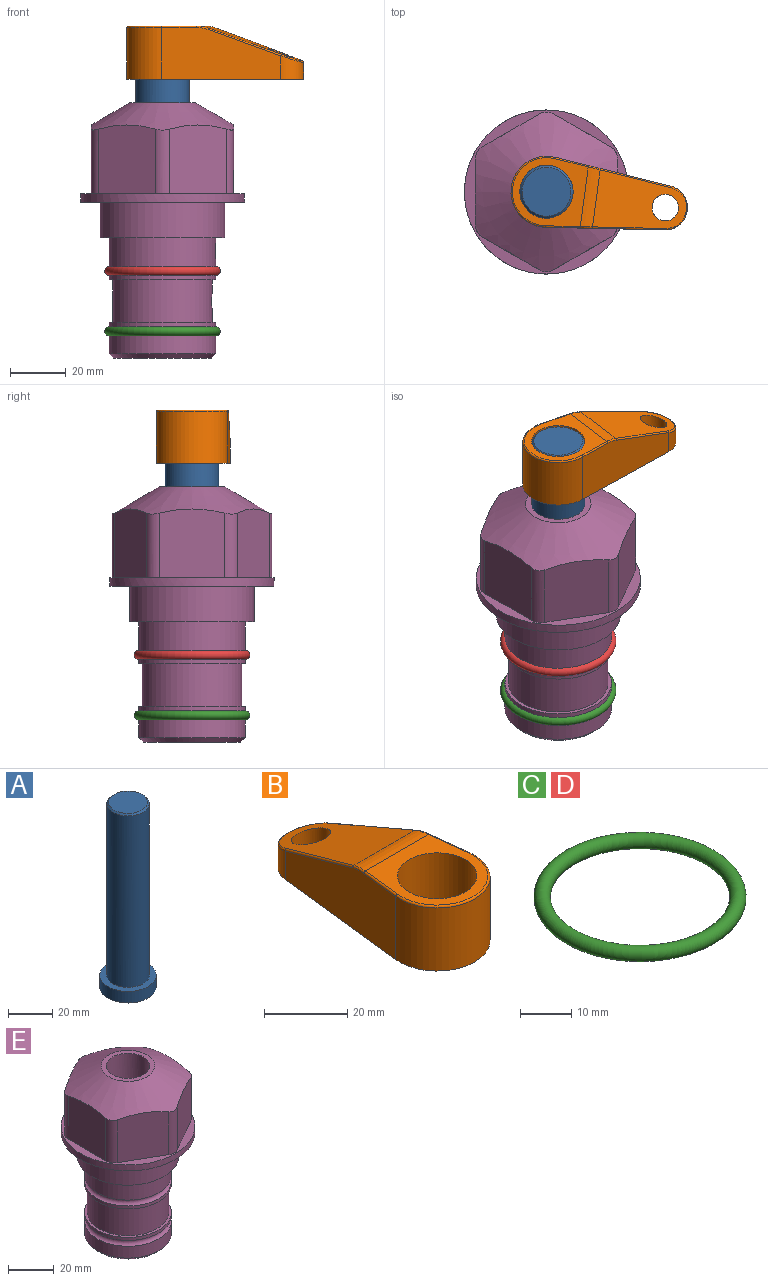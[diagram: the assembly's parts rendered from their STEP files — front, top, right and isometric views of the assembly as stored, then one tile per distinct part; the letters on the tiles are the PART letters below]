
ASSEMBLY  parts=5 mates=3
PART A: 6 faces, bbox 25.4x25.4x101.6 mm
  f0: plane 17.46x17.46mm, normal (0,0,1), area 239.5mm2, adj f5
  f1: plane 25.4x25.4mm, normal (0,0,-1), area 506.7mm2, adj f2
  f2: cylinder r=12.7mm len=25.4mm, axis (0,0,1), area 506.7mm2, adj f1,f3
  f3: plane 25.4x25.4mm, normal (0,0,1), area 221.7mm2, adj f2,f4
  f4: cylinder r=9.53mm len=94.46mm, axis (0,0,1), area 5653mm2, adj f3,f5
  f5: cone r=8.73mm half-angle=45deg, axis (0,0,-1), area 64.4mm2, adj f0,f4
PART B: 44 faces, bbox 27.5x64.5x19.1 mm
  f0: plane 2.3x0.95mm, normal (0,0,-1), area 1mm2, adj f25,f30,f34
  f1: plane 63.5x25.4mm, normal (0,0,-1), area 561.7mm2, adj f2,f3,f4,f5,f6,f7,f19,f20
  f2: cylinder r=12.7mm len=25.4mm, axis (0,0,-1), area 792.2mm2, adj f1,f3,f5,f13
  f3: plane 42.33x18.54mm, normal (0.99,0.11,0), area 647mm2, adj f1,f2,f4,f11,f12,f14
  f4: cylinder r=7.94mm len=15.78mm, axis (0,0,-1), area 158.6mm2, adj f1,f3,f5,f16
  f5: plane 42.33x18.54mm, normal (-0.99,0.11,0), area 647mm2, adj f1,f2,f4,f15,f17,f18
  f6: cylinder r=9.53mm len=19.05mm, axis (0,0,-1), area 1140.1mm2, adj f1,f8
  f7: cylinder r=4.76mm len=10.98mm, axis (0,0,-1), area 276.1mm2, adj f1,f9
  f8: plane 25.83x24.38mm, normal (0,0,1), area 262.2mm2, adj f6,f10,f11,f13,f15
  f9: plane 32.49x20.55mm, normal (0,0.34,0.94), area 489.9mm2, adj f7,f10,f14,f16,f18
  f10: cylinder r=12.7mm len=21.49mm, axis (-1,0,0), area 93.2mm2, adj f8,f9,f12,f17
  f11: cylinder r=0.51mm len=12.34mm, axis (0.11,-0.99,0), area 9.9mm2, adj f3,f8,f12,f13
  f12: bspline ~7.62x1.64mm, area 3.5mm2, adj f3,f10,f11,f14
  f13: torus R=12.19mm, axis (0,0,1), area 33.6mm2, adj f2,f8,f11,f15
  f14: cylinder r=0.51mm len=26.01mm, axis (0.1,-0.93,0.34), area 21.6mm2, adj f3,f9,f12,f16
  f15: cylinder r=0.51mm len=12.34mm, axis (0.11,0.99,0), area 9.9mm2, adj f5,f8,f13,f17
  f16: bspline ~15.78x7.05mm, area 15.7mm2, adj f4,f9,f14,f18
  f17: bspline ~7.62x1.64mm, area 3.5mm2, adj f5,f10,f15,f18
  f18: cylinder r=0.51mm len=26.01mm, axis (0.1,0.93,-0.34), area 21.6mm2, adj f5,f9,f16,f17
  f19: plane 21.6x14.29mm, normal (-0.99,-0.11,0), area 242.6mm2, adj f1,f26,f28,f34,f36,f38
  f20: plane 21.6x14.29mm, normal (0.99,-0.11,0), area 242.6mm2, adj f1,f27,f29,f37,f39,f41
  f21: cylinder r=12.7mm len=14.29mm, axis (0,0,-1), area 173.2mm2, adj f1,f26,f27,f30,f31,f33
  f22: cylinder r=7.94mm len=7.63mm, axis (0,0,-1), area 53.8mm2, adj f1,f28,f29,f42
  f23: plane 2.3x0.95mm, normal (0,0,-1), area 1mm2, adj f25,f33,f37
  f24: plane 17.94x12.32mm, normal (0,-0.34,-0.94), area 191.2mm2, adj f25,f38,f41,f42
  f25: cylinder r=9.53mm len=12.93mm, axis (-1,0,0), area 37.5mm2, adj f0,f23,f24,f31,f36,f39
  f26: cylinder r=1.59mm len=14.29mm, axis (0,0,-1), area 49mm2, adj f1,f19,f21,f32
  f27: cylinder r=1.59mm len=14.29mm, axis (0,0,-1), area 49mm2, adj f1,f20,f21,f35
  f28: cylinder r=1.59mm len=7.28mm, axis (0,0,-1), area 22.1mm2, adj f1,f19,f22,f40
  f29: cylinder r=1.59mm len=7.28mm, axis (0,0,-1), area 22.1mm2, adj f1,f20,f22,f43
  f30: torus R=14.29mm, axis (0,0,1), area 5.8mm2, adj f0,f21,f31,f32
  f31: bspline ~11.06x2.73mm, area 20.8mm2, adj f21,f25,f30,f33
  f32: sphere r=1.59mm, area 5.4mm2, adj f26,f30,f34
  f33: torus R=14.29mm, axis (0,0,1), area 5.8mm2, adj f21,f23,f31,f35
  f34: cylinder r=1.59mm len=1.68mm, axis (-0.11,0.99,0), area 2.4mm2, adj f0,f19,f32,f36
  f35: sphere r=1.59mm, area 5.4mm2, adj f27,f33,f37
  f36: bspline ~5.82x2.33mm, area 7.7mm2, adj f19,f25,f34,f38
  f37: cylinder r=1.59mm len=1.68mm, axis (0.11,0.99,0), area 2.4mm2, adj f20,f23,f35,f39
  f38: cylinder r=1.59mm len=18.33mm, axis (0.1,-0.93,0.34), area 46.7mm2, adj f19,f24,f36,f40
  f39: bspline ~5.82x2.33mm, area 7.7mm2, adj f20,f25,f37,f41
  f40: sphere r=1.59mm, area 3.6mm2, adj f28,f38,f42
  f41: cylinder r=1.59mm len=18.33mm, axis (0.1,0.93,-0.34), area 46.7mm2, adj f20,f24,f39,f43
  f42: bspline ~8.31x1.84mm, area 15.3mm2, adj f22,f24,f40,f43
  f43: sphere r=1.59mm, area 3.6mm2, adj f29,f41,f42
PART C: 1 faces, bbox 44.7x44.7x3.2 mm
  f0: torus R=19.05mm, axis (0,0,1), area 1193.9mm2
PART D: same geometry as C
PART E: 36 faces, bbox 58.7x58.7x91.2 mm
  f0: cylinder r=17.78mm len=35.56mm, axis (0,0,1), area 1670.8mm2, adj f23,f24,f31
  f1: cylinder r=19.05mm len=38.1mm, axis (0,0,1), area 1191.9mm2, adj f26,f27,f30
  f2: plane 58.66x58.66mm, normal (0,0,-1), area 1150.6mm2, adj f3,f28
  f3: cylinder r=29.33mm len=58.66mm, axis (0,0,-1), area 585.1mm2, adj f2,f4
  f4: plane 58.66x58.66mm, normal (0,0,1), area 475.9mm2, adj f3,f5,f6,f7,f8,f9,f10,f11
  f5: plane 24.5x20.32mm, normal (-0.5,0.87,0), area 562.8mm2, adj f4,f15,f16,f17
  f6: plane 24.5x20.32mm, normal (0.5,0.87,0), area 562.8mm2, adj f4,f14,f15,f17
  f7: plane 24.5x23.48mm, normal (1,0,0), area 562.8mm2, adj f4,f13,f14,f17
  f8: plane 24.5x20.32mm, normal (0.5,-0.87,0), area 562.8mm2, adj f4,f12,f13,f17
  f9: plane 24.5x20.32mm, normal (-0.5,-0.87,0), area 562.8mm2, adj f4,f11,f12,f17
  f10: plane 24.5x23.48mm, normal (-1,0,0), area 562.8mm2, adj f4,f11,f16,f17
  f11: cylinder r=5.08mm len=23.01mm, axis (0,0,-1), area 121.2mm2, adj f4,f9,f10,f17
  f12: cylinder r=5.08mm len=23.01mm, axis (0,0,-1), area 121.2mm2, adj f4,f8,f9,f17
  f13: cylinder r=5.08mm len=23.01mm, axis (0,0,-1), area 121.2mm2, adj f4,f7,f8,f17
  f14: cylinder r=5.08mm len=23.01mm, axis (0,0,-1), area 121.2mm2, adj f4,f6,f7,f17
  f15: cylinder r=5.08mm len=23.01mm, axis (0,0,-1), area 121.2mm2, adj f4,f5,f6,f17
  f16: cylinder r=5.08mm len=23.01mm, axis (0,0,-1), area 121.2mm2, adj f4,f5,f10,f17
  f17: cone r=11.73mm half-angle=60deg, axis (0,0,-1), area 2071.8mm2, adj f5,f6,f7,f8,f9,f10,f11,f12
  f18: plane 23.46x23.46mm, normal (0,0,1), area 147.4mm2, adj f17,f35
  f19: plane 34.93x34.93mm, normal (0,0,-1), area 958mm2, adj f29
  f20: cylinder r=19.05mm len=38.1mm, axis (0,0,1), area 760.1mm2, adj f21,f29
  f21: torus R=19.05mm, axis (0,0,1), area 565.3mm2, adj f20,f22
  f22: cylinder r=19.05mm len=38.1mm, axis (0,0,1), area 190mm2, adj f21,f23
  f23: plane 38.1x38.1mm, normal (0,0,1), area 146.9mm2, adj f0,f22
  f24: plane 38.1x38.1mm, normal (0,0,-1), area 146.9mm2, adj f0,f25
  f25: cylinder r=19.05mm len=38.1mm, axis (0,0,1), area 190mm2, adj f24,f26
  f26: torus R=19.05mm, axis (0,0,1), area 565.3mm2, adj f1,f25
  f27: plane 44.45x44.45mm, normal (0,0,-1), area 411.7mm2, adj f1,f28
  f28: cylinder r=22.23mm len=44.45mm, axis (0,0,1), area 1773.5mm2, adj f2,f27
  f29: cone r=19.05mm half-angle=45deg, axis (0,0,1), area 257.5mm2, adj f19,f20
  f30: cylinder r=3.17mm len=6.75mm, axis (-1,0,0), area 128mm2, adj f1,f33
  f31: cylinder r=3.17mm len=6.35mm, axis (-1,0,0), area 102.5mm2, adj f0,f33
  f32: plane 25.4x25.4mm, normal (0,0,1), area 506.7mm2, adj f33
  f33: cylinder r=12.7mm len=66.42mm, axis (0,0,-1), area 5236.2mm2, adj f30,f31,f32,f34
  f34: cone r=9.53mm half-angle=30deg, axis (0,0,-1), area 443.4mm2, adj f33,f35
  f35: cylinder r=9.53mm len=19.05mm, axis (0,0,-1), area 849mm2, adj f18,f34
PLACE A rot(axis=(0,0,-1),7.6deg) t=(0,0,-10.61)mm
PLACE B rot(axis=(0,0,-1),97.6deg) t=(0,0,44)mm
PLACE C t=(0,0,-21.59)mm
PLACE D at identity
PLACE E at identity fixed
MATE fastened C.f0 <-> E.f0  axis (0,0,1) through (0,0,-46.1)mm
MATE cylindrical A.f2 <-> E.f0  axis (0,0,1) through (0,0,15.03)mm
MATE fastened B.f2 <-> A.f2  axis (0,0,1) through (0,0,63.05)mm
